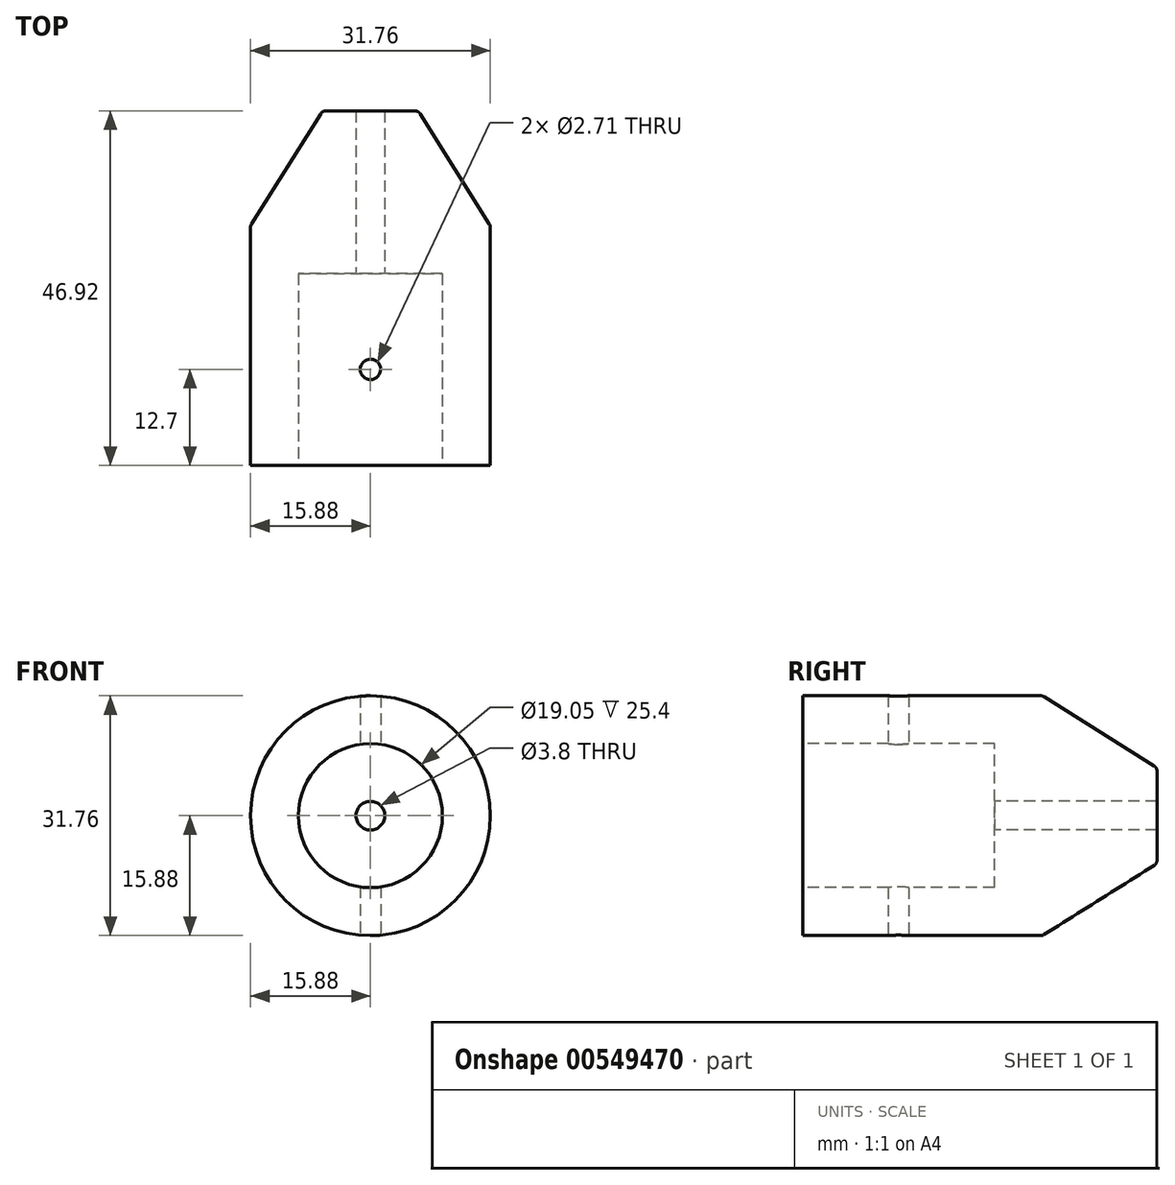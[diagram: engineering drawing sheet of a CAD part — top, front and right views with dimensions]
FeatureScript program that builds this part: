
annotation { "Feature Type Name" : "Feature", "Feature Type Description" : "" }
export const myFeature = defineFeature(function(context is Context, id is Id, definition is map)
    precondition{}
    {
        {
            var Q0;
            Q0=qCreatedBy(makeId("Right.planeOp"),FACE);
            var sketch = newSketch(context, id + "F0", { "sketchPlane" : qUnion([Q0])});
            skLineSegment(sketch, "E0", {"start": v(-31.75, 15.87) * mm, "end": v(0, 15.88) * mm});
            skLineSegment(sketch, "E1", {"start": v(-31.75, 15.87) * mm, "end": v(-31.75, 9.53) * mm});
            skLineSegment(sketch, "E2", {"start": v(-31.75, 9.53) * mm, "end": v(-6.35, 9.53) * mm});
            skLineSegment(sketch, "E3", {"start": v(-6.35, 9.53) * mm, "end": v(-6.35, 0) * mm});
            skLineSegment(sketch, "E4", {"start": v(-6.35, 0) * mm, "end": v(15.17, 0) * mm});
            skLineSegment(sketch, "E5", {"start": v(15.17, 0) * mm, "end": v(15.17, 6.35) * mm});
            skLineSegment(sketch, "E6", {"start": v(0, 15.88) * mm, "end": v(15.17, 6.35) * mm});
            skSolve(sketch);
        }
        {
            var Q0;
            Q0 = qSketchRegion(id + "F0", true);
            var Q1;
            Q1=sQuery(id+"F0.wireOp",EDGE,"E4");
            revolve(context, id + "F1", {"entities" : qUnion([Q0]), "axis" : qUnion([Q1]), "revolveType" : RevolveType.FULL});
        }
        {
            var Q0;
            Q0=makeQuery(id+"F1.opRevolve","SWEPT_FACE",FACE,{"disambiguationData":[OSD([sQuery(id+"F0.wireOp",EDGE,"E5")])]});
            var sketch = newSketch(context, id + "F2", { "sketchPlane" : qUnion([Q0])});
            skPoint(sketch, "E7.0", {"position": v(0, 0) * mm});
            skSolve(sketch);
        }
        {
            var Q0;
            Q0=sQuery(id+"F2.wireOp",VERTEX,"E7.0");
            var Q1;
            Q1=makeQuery(id+"F1.opRevolve","SWEPT_BODY",BODY,{"disambiguationData":[OSD([sQuery(id+"F0.wireOp",EDGE,"E0"),sQuery(id+"F0.wireOp",EDGE,"E1"),sQuery(id+"F0.wireOp",EDGE,"E2"),sQuery(id+"F0.wireOp",EDGE,"E3"),sQuery(id+"F0.wireOp",EDGE,"E4"),sQuery(id+"F0.wireOp",EDGE,"w9dLrYv9-lBM8-68nR-eK5x-by8z1ml0Crkc"),sQuery(id+"F0.wireOp",EDGE,"wdY8MxJK-PCpl-DHCc-kkbj-PTYJsvz9WHpY")])]});
            hole(context, id + "F3", {"style" : HoleStyle.SIMPLE, "endStyle" : HoleEndStyle.THROUGH, "standardTappedOrClearance" : lookupTablePath({ "standard" : "ANSI", "engagement" : "75%", "pitch" : "24 tpi", "size" : "#10", "type" : "Tapped" }), "standardBlindInLast" : lookupTablePath({ "standard" : "ANSI", "engagement" : "75%", "pitch" : "24 tpi", "size" : "#10", "type" : "Tapped" }), "holeDiameter" : 3.8 * mm, "majorDiameter" : 4.83 * mm, "showTappedDepth" : true, "tappedDepth" : 15.24 * mm, "tapClearance" : 3, "startFromSketch" : true, "locations" : qUnion([Q0]), "scope" : qUnion([Q1])});
        }
        {
            var Q0;
            Q0=qCreatedBy(makeId("Top.planeOp"),FACE);
            cPlane(context, id + "F4", {"entities" : qUnion([Q0]), "cplaneType" : CPlaneType.OFFSET, "offset" : 17.02 * mm, "width" : 152.4 * mm, "height" : 152.4 * mm});
        }
        {
            var Q0;
            Q0=qCreatedBy(id+"F4.planeOp",FACE);
            var sketch = newSketch(context, id + "F5", { "sketchPlane" : qUnion([Q0])});
            skLineSegment(sketch, "E8", {"start": v(-15.88, -35.63) * mm, "end": v(-15.88, -2.47) * mm});
            skLineSegment(sketch, "E9", {"start": v(15.88, 0) * mm, "end": v(15.88, -35.63) * mm});
            skPoint(sketch, "E10", {"position": v(0, -19.05) * mm});
            skPoint(sketch, "E10.positionSnap0", {"position": v(-15.88, -19.05) * mm});
            skSolve(sketch);
        }
        {
            var Q0;
            Q0=sQuery(id+"F5.wireOp",VERTEX,"E10");
            var Q1;
            Q1=makeQuery(id+"F1.opRevolve","SWEPT_BODY",BODY,{"disambiguationData":[OSD([sQuery(id+"F0.wireOp",EDGE,"E0"),sQuery(id+"F0.wireOp",EDGE,"E1"),sQuery(id+"F0.wireOp",EDGE,"E2"),sQuery(id+"F0.wireOp",EDGE,"E3"),sQuery(id+"F0.wireOp",EDGE,"E4"),sQuery(id+"F0.wireOp",EDGE,"E5"),sQuery(id+"F0.wireOp",EDGE,"E6")])]});
            hole(context, id + "F6", {"style" : HoleStyle.SIMPLE, "endStyle" : HoleEndStyle.THROUGH, "standardTappedOrClearance" : lookupTablePath({ "standard" : "ANSI", "engagement" : "75%", "pitch" : "32 tpi", "size" : "#6", "type" : "Tapped" }), "standardBlindInLast" : lookupTablePath({ "standard" : "ANSI", "engagement" : "75%", "pitch" : "32 tpi", "size" : "#6", "type" : "Tapped" }), "holeDiameter" : 2.7 * mm, "majorDiameter" : 3.5 * mm, "showTappedDepth" : true, "isTappedThrough" : true, "tappedDepth" : 15.24 * mm, "tapClearance" : 3, "startFromSketch" : true, "locations" : qUnion([Q0]), "scope" : qUnion([Q1])});
        }
        {
            var Q0;
            Q0=makeQuery(id+"F1.opRevolve","SWEPT_EDGE",EDGE,{"disambiguationData":[OSD([sQuery(id+"F0.wireOp",EDGE,"E5"),sQuery(id+"F0.wireOp",EDGE,"E6")])]});
            var Q1;
            Q1=makeQuery(id+"F1.opRevolve","SWEPT_EDGE",EDGE,{"disambiguationData":[OSD([sQuery(id+"F0.wireOp",EDGE,"E0"),sQuery(id+"F0.wireOp",EDGE,"E6")])]});
            fillet(context, id + "F7", {"entities" : qUnion([Q0, Q1]), "radius" : 0.76 * mm, "tangentPropagation" : true, "allowEdgeOverflow" : false});
        }
    });
